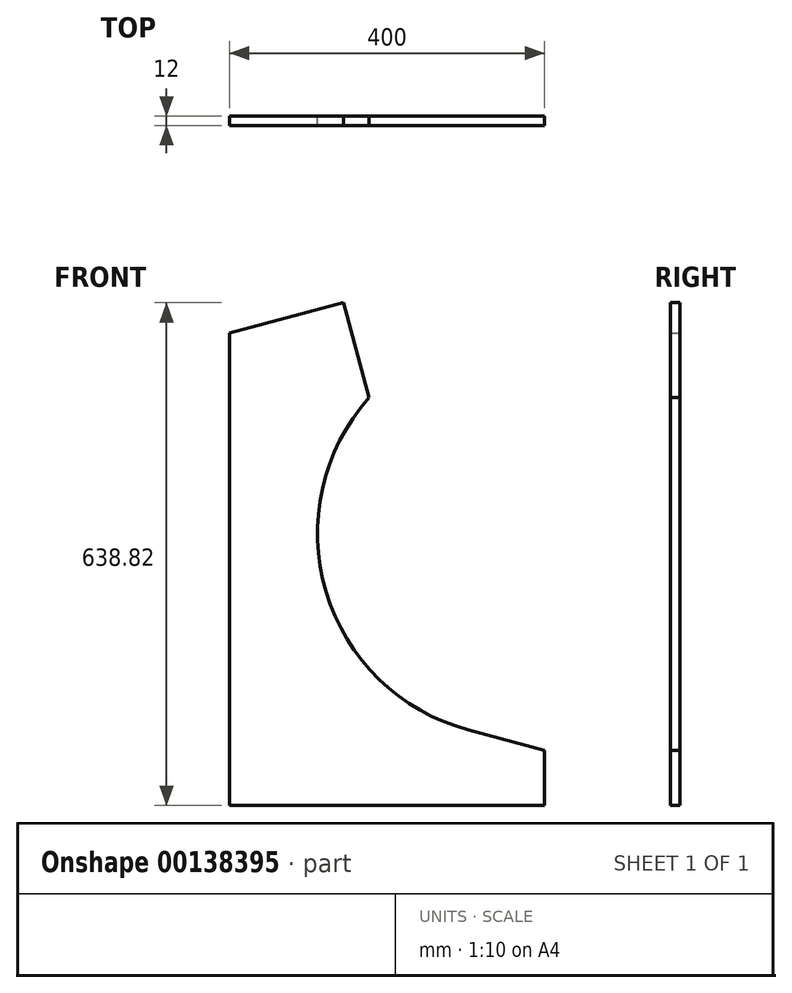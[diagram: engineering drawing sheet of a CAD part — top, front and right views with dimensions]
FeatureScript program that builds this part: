
annotation { "Feature Type Name" : "Feature", "Feature Type Description" : "" }
export const myFeature = defineFeature(function(context is Context, id is Id, definition is map)
    precondition{}
    {
        {
            var Q0;
            Q0=qCreatedBy(makeId("Front.planeOp"),FACE);
            var sketch = newSketch(context, id + "F0", { "sketchPlane" : qUnion([Q0])});
            skLineSegment(sketch, "E0", {"start": v(0, 0) * mm, "end": v(400, 0) * mm});
            skLineSegment(sketch, "E1", {"start": v(0, 0) * mm, "end": v(0, 600) * mm});
            skLineSegment(sketch, "E2", {"start": v(0, 600) * mm, "end": v(144.89, 638.82) * mm});
            skLineSegment(sketch, "E3", {"start": v(144.89, 638.82) * mm, "end": v(177.24, 518.08) * mm});
            skLineSegment(sketch, "E4", {"start": v(400, 0) * mm, "end": v(400, 70) * mm});
            skLineSegment(sketch, "E5", {"start": v(400, 70) * mm, "end": v(303.4, 95.88) * mm});
            skArc(sketch, "E6", {"start": v(303.4, 95.88) * mm, "mid": v(122.44, 271.75) * mm, "end": v(177.24, 518.08) * mm});
            skSolve(sketch);
        }
        {
            var Q0;
            Q0 = qSketchRegion(id + "F0", true);
            extrude(context, id + "F1", {"entities" : qUnion([Q0]), "depth" : 12 * mm});
        }
    });
